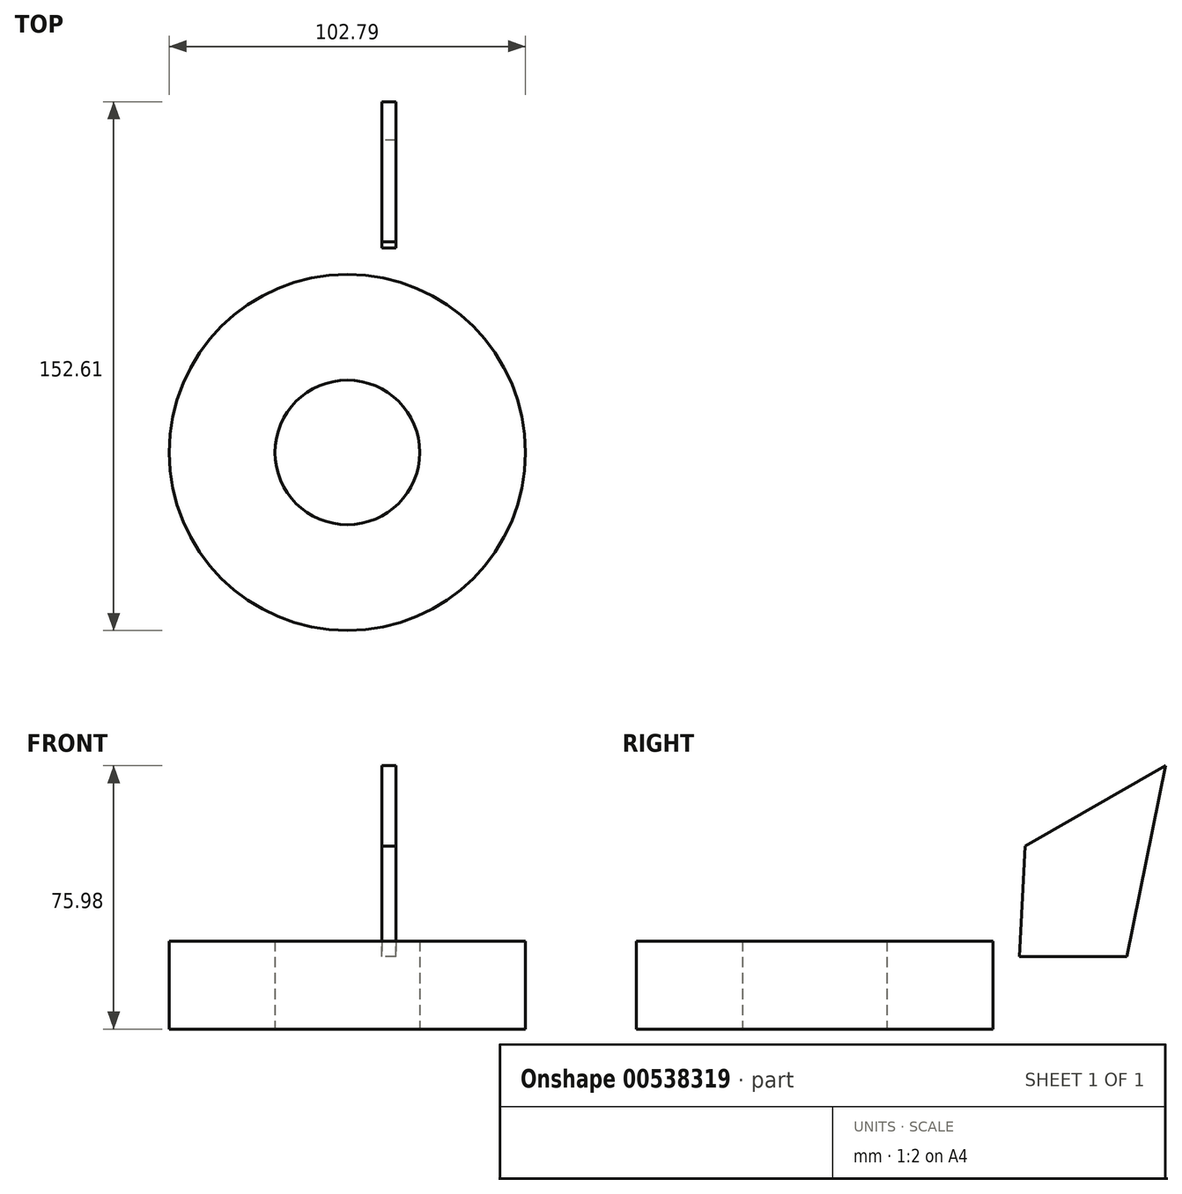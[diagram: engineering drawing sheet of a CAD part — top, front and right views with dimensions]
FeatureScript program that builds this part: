
annotation { "Feature Type Name" : "Feature", "Feature Type Description" : "" }
export const myFeature = defineFeature(function(context is Context, id is Id, definition is map)
    precondition{}
    {
        {
            var Q0;
            Q0=qCreatedBy(makeId("Top.planeOp"),FACE);
            var sketch = newSketch(context, id + "F0", { "sketchPlane" : qUnion([Q0])});
            skCircle(sketch, "E0", {"center": v(-9.93, -174.98) * mm, "radius": 51.4 * mm});
            skCircle(sketch, "E1", {"center": v(-9.93, -174.98) * mm, "radius": 20.86 * mm});
            skSolve(sketch);
        }
        {
            var Q0;
            Q0=makeQuery(id+"F0.imprint","IMPRINT",FACE,{"disambiguationData":[TD([[makeQuery(id+"F0.imprint","IMPRINT",EDGE,{"derivedFrom":sQuery(id+"F0.wireOp",EDGE,"E0")}),1.0]])]});
            extrude(context, id + "F1", {"entities" : qUnion([Q0]), "depth" : 25.4 * mm, "offsetDistance" : 25.4 * mm});
        }
        {
            var Q0;
            Q0=qCreatedBy(makeId("Right.planeOp"),FACE);
            var sketch = newSketch(context, id + "F2", { "sketchPlane" : qUnion([Q0])});
            skLineSegment(sketch, "E2", {"start": v(-115.98, 20.88) * mm, "end": v(-84.9, 20.88) * mm});
            skLineSegment(sketch, "E3", {"start": v(-84.9, 20.88) * mm, "end": v(-73.77, 75.98) * mm});
            skLineSegment(sketch, "E4", {"start": v(-73.77, 75.98) * mm, "end": v(-114.22, 52.82) * mm});
            skLineSegment(sketch, "E5", {"start": v(-114.22, 52.82) * mm, "end": v(-115.98, 20.88) * mm});
            skSolve(sketch);
        }
        {
            var Q0;
            Q0=makeQuery(id+"F2.imprint","IMPRINT",FACE,{"disambiguationData":[TD([[makeQuery(id+"F2.imprint","IMPRINT",EDGE,{"derivedFrom":sQuery(id+"F2.wireOp",EDGE,"E2")}),1.0]])]});
            extrude(context, id + "F3", {"entities" : qUnion([Q0]), "depth" : 4.06 * mm, "offsetDistance" : 25.4 * mm});
        }
    });
